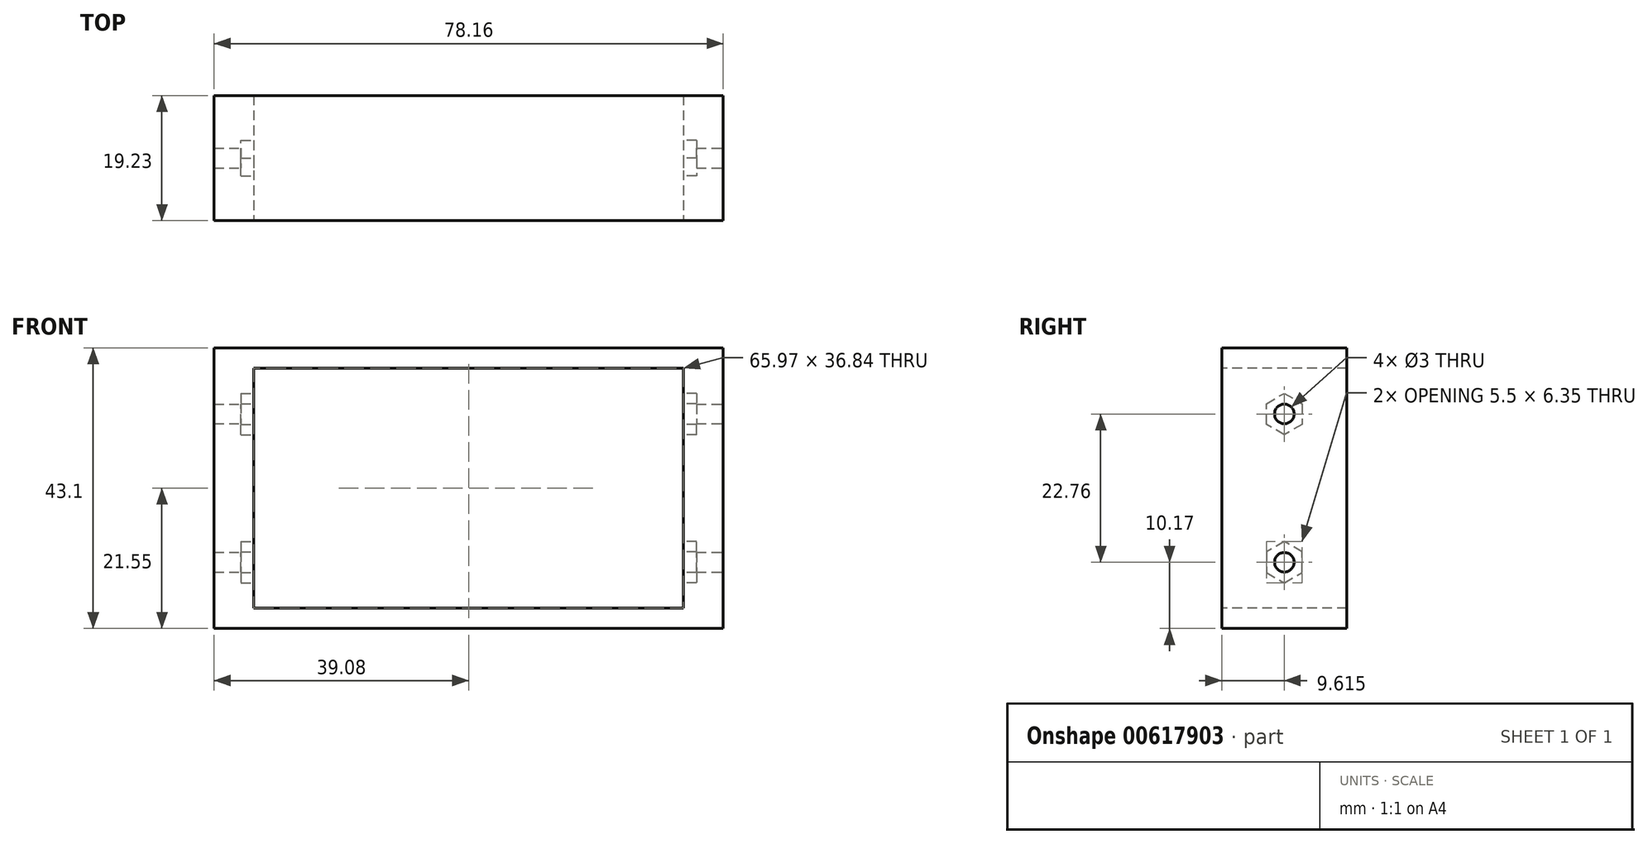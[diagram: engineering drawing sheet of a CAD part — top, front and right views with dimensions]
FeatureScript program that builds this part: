
annotation { "Feature Type Name" : "Feature", "Feature Type Description" : "" }
export const myFeature = defineFeature(function(context is Context, id is Id, definition is map)
    precondition{}
    {
        {
            var Q0;
            Q0=qCreatedBy(makeId("Front.planeOp"),FACE);
            var sketch = newSketch(context, id + "F0", { "sketchPlane" : qUnion([Q0])});
            skLineSegment(sketch, "E0.bottom", {"start": v(-39.07, 21.55) * mm, "end": v(39.08, 21.55) * mm});
            skLineSegment(sketch, "E0.top", {"start": v(-39.08, -21.55) * mm, "end": v(39.07, -21.55) * mm});
            skLineSegment(sketch, "E0.left", {"start": v(-39.07, 21.55) * mm, "end": v(-39.08, -21.55) * mm});
            skLineSegment(sketch, "E0.right", {"start": v(39.08, 21.55) * mm, "end": v(39.07, -21.55) * mm});
            skPoint(sketch, "E0.middle", {"position": v(0, 0) * mm});
            skSolve(sketch);
        }
        {
            var Q0;
            Q0=makeQuery(id+"F0.imprint","IMPRINT",FACE,{"disambiguationData":[TD([[makeQuery(id+"F0.imprint","IMPRINT",EDGE,{"derivedFrom":sQuery(id+"F0.wireOp",EDGE,"E0.bottom")}),-1.0]])]});
            extrude(context, id + "F1", {"entities" : qUnion([Q0]), "depth" : 19.23 * mm, "offsetDistance" : 25 * mm});
        }
        {
            var Q0;
            Q0=makeQuery(id+"F1.opExtrude","CAP_FACE",FACE,{"disambiguationData":[OSD([sQuery(id+"F0.wireOp",EDGE,"E0.bottom"),sQuery(id+"F0.wireOp",EDGE,"E0.top"),sQuery(id+"F0.wireOp",EDGE,"E0.left"),sQuery(id+"F0.wireOp",EDGE,"E0.right")])],"isStart":false});
            var sketch = newSketch(context, id + "F2", { "sketchPlane" : qUnion([Q0])});
            skLineSegment(sketch, "E1.bottom", {"start": v(-32.98, -18.42) * mm, "end": v(32.98, -18.42) * mm});
            skLineSegment(sketch, "E1.top", {"start": v(-32.98, 18.42) * mm, "end": v(32.98, 18.42) * mm});
            skLineSegment(sketch, "E1.left", {"start": v(-32.98, -18.42) * mm, "end": v(-32.98, 18.42) * mm});
            skLineSegment(sketch, "E1.right", {"start": v(32.98, -18.42) * mm, "end": v(32.98, 18.42) * mm});
            skPoint(sketch, "E1.middle", {"position": v(0, 0) * mm});
            skSolve(sketch);
        }
        {
            var Q0;
            Q0=makeQuery(id+"F2.imprint","IMPRINT",FACE,{"disambiguationData":[TD([[makeQuery(id+"F2.imprint","IMPRINT",EDGE,{"derivedFrom":sQuery(id+"F2.wireOp",EDGE,"E1.bottom")}),1.0]])]});
            extrude(context, id + "F3", {"entities" : qUnion([Q0]), "operationType" : NewBodyOperationType.REMOVE, "oppositeDirection" : true, "depth" : 35 * mm, "offsetDistance" : 25 * mm});
        }
        {
            var Q0;
            Q0=makeQuery(id+"F1.opExtrude","SWEPT_FACE",FACE,{"disambiguationData":[OSD([sQuery(id+"F0.wireOp",EDGE,"E0.right")])]});
            var sketch = newSketch(context, id + "F4", { "sketchPlane" : qUnion([Q0])});
            skCircle(sketch, "E2", {"center": v(-9.62, 11.38) * mm, "radius": 1.5 * mm});
            skCircle(sketch, "E3", {"center": v(-9.62, -11.38) * mm, "radius": 1.5 * mm});
            skSolve(sketch);
        }
        {
            var Q0;
            Q0=makeQuery(id+"F4.imprint","IMPRINT",FACE,{"disambiguationData":[TD([[makeQuery(id+"F4.imprint","IMPRINT",EDGE,{"derivedFrom":sQuery(id+"F4.wireOp",EDGE,"E2")}),1.0]])]});
            var Q1;
            Q1=makeQuery(id+"F4.imprint","IMPRINT",FACE,{"disambiguationData":[TD([[makeQuery(id+"F4.imprint","IMPRINT",EDGE,{"derivedFrom":sQuery(id+"F4.wireOp",EDGE,"E3")}),1.0]])]});
            extrude(context, id + "F5", {"entities" : qUnion([Q0, Q1]), "operationType" : NewBodyOperationType.REMOVE, "oppositeDirection" : true, "depth" : 100000 * mm, "offsetDistance" : 25 * mm});
        }
        {
            var Q0;
            Q0=makeQuery(id+"F3.boolean.opBoolean","COPY",FACE,{"derivedFrom":makeQuery(id+"F3.opExtrude","SWEPT_FACE",FACE,{"disambiguationData":[OSD([sQuery(id+"F2.wireOp",EDGE,"E1.left")])]})});
            var sketch = newSketch(context, id + "F6", { "sketchPlane" : qUnion([Q0])});
            skCircle(sketch, "E4.cCircle", {"center": v(-9.62, 11.38) * mm, "radius": 2.75 * mm, "construction": true});
            skLineSegment(sketch, "E4.0", {"start": v(-6.87, 12.97) * mm, "end": v(-6.87, 9.8) * mm});
            skLineSegment(sketch, "E4.1", {"start": v(-6.87, 9.8) * mm, "end": v(-9.62, 8.2) * mm});
            skLineSegment(sketch, "E4.2", {"start": v(-9.62, 8.2) * mm, "end": v(-12.36, 9.8) * mm});
            skLineSegment(sketch, "E4.3", {"start": v(-12.36, 9.8) * mm, "end": v(-12.36, 12.97) * mm});
            skLineSegment(sketch, "E4.4", {"start": v(-12.36, 12.97) * mm, "end": v(-9.62, 14.56) * mm});
            skLineSegment(sketch, "E4.5", {"start": v(-9.62, 14.56) * mm, "end": v(-6.87, 12.97) * mm});
            skPoint(sketch, "E4.0.midPoint", {"position": v(-6.87, 11.38) * mm});
            skLineSegment(sketch, "E5.MirrorCS", {"start": v(-9.62, -14.56) * mm, "end": v(-6.87, -12.97) * mm});
            skLineSegment(sketch, "E6.MirrorCS", {"start": v(-6.87, -12.97) * mm, "end": v(-6.87, -9.8) * mm});
            skLineSegment(sketch, "E7.MirrorCS", {"start": v(-9.62, -8.2) * mm, "end": v(-12.36, -9.8) * mm});
            skCircle(sketch, "E8.MirrorC", {"center": v(-9.62, -11.38) * mm, "radius": 2.75 * mm, "construction": true});
            skLineSegment(sketch, "E9.MirrorCS", {"start": v(-12.36, -9.8) * mm, "end": v(-12.36, -12.97) * mm});
            skLineSegment(sketch, "E10.MirrorCS", {"start": v(-12.36, -12.97) * mm, "end": v(-9.62, -14.56) * mm});
            skLineSegment(sketch, "E11.MirrorCS", {"start": v(-6.87, -9.8) * mm, "end": v(-9.62, -8.2) * mm});
            skPoint(sketch, "E12.MirrorP", {"position": v(-6.87, -11.38) * mm});
            skSolve(sketch);
        }
        {
            var Q0;
            Q0=makeQuery(id+"F3.boolean.opBoolean","COPY",FACE,{"derivedFrom":makeQuery(id+"F3.opExtrude","SWEPT_FACE",FACE,{"disambiguationData":[OSD([sQuery(id+"F2.wireOp",EDGE,"E1.right")])]})});
            var sketch = newSketch(context, id + "F7", { "sketchPlane" : qUnion([Q0])});
            skCircle(sketch, "E13.cCircle", {"center": v(9.62, 11.38) * mm, "radius": 2.75 * mm, "construction": true});
            skLineSegment(sketch, "E13.0", {"start": v(12.37, 12.97) * mm, "end": v(12.37, 9.8) * mm});
            skLineSegment(sketch, "E13.1", {"start": v(12.37, 9.8) * mm, "end": v(9.62, 8.2) * mm});
            skLineSegment(sketch, "E13.2", {"start": v(9.62, 8.2) * mm, "end": v(6.86, 9.8) * mm});
            skLineSegment(sketch, "E13.3", {"start": v(6.86, 9.8) * mm, "end": v(6.86, 12.97) * mm});
            skLineSegment(sketch, "E13.4", {"start": v(6.86, 12.97) * mm, "end": v(9.61, 14.56) * mm});
            skLineSegment(sketch, "E13.5", {"start": v(9.61, 14.56) * mm, "end": v(12.37, 12.97) * mm});
            skPoint(sketch, "E13.0.midPoint", {"position": v(12.37, 11.38) * mm});
            skLineSegment(sketch, "E14.MirrorCS", {"start": v(9.61, -14.56) * mm, "end": v(12.37, -12.97) * mm});
            skLineSegment(sketch, "E15.MirrorCS", {"start": v(6.86, -12.97) * mm, "end": v(9.61, -14.56) * mm});
            skLineSegment(sketch, "E16.MirrorCS", {"start": v(6.86, -9.8) * mm, "end": v(6.86, -12.97) * mm});
            skLineSegment(sketch, "E17.MirrorCS", {"start": v(9.62, -8.2) * mm, "end": v(6.86, -9.8) * mm});
            skLineSegment(sketch, "E18.MirrorCS", {"start": v(12.37, -9.8) * mm, "end": v(9.62, -8.2) * mm});
            skCircle(sketch, "E19.MirrorC", {"center": v(9.62, -11.38) * mm, "radius": 2.75 * mm, "construction": true});
            skLineSegment(sketch, "E20.MirrorCS", {"start": v(12.37, -12.97) * mm, "end": v(12.37, -9.8) * mm});
            skPoint(sketch, "E21.MirrorP", {"position": v(12.37, -11.38) * mm});
            skSolve(sketch);
        }
        {
            var Q0;
            Q0 = qSketchRegion(id + "F7", true);
            extrude(context, id + "F8", {"entities" : qUnion([Q0]), "operationType" : NewBodyOperationType.REMOVE, "oppositeDirection" : true, "depth" : 2 * mm, "offsetDistance" : 25 * mm});
        }
        {
            var Q0;
            Q0 = qSketchRegion(id + "F6", true);
            extrude(context, id + "F9", {"entities" : qUnion([Q0]), "operationType" : NewBodyOperationType.REMOVE, "oppositeDirection" : true, "depth" : 2 * mm, "offsetDistance" : 25 * mm});
        }
    });
